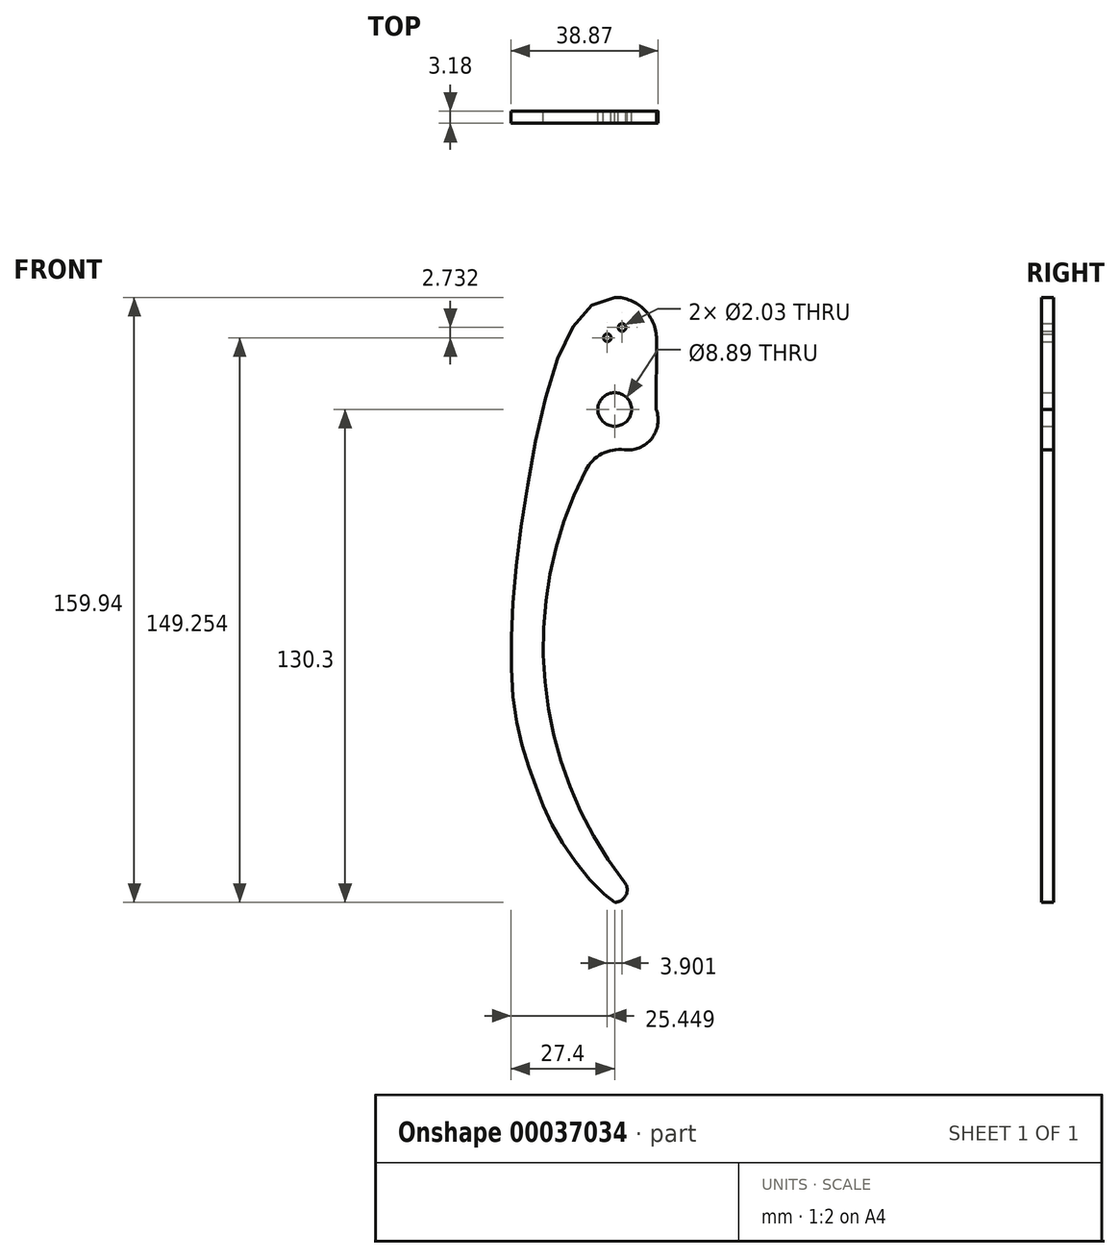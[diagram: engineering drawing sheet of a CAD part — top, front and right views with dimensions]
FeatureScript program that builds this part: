
annotation { "Feature Type Name" : "Feature", "Feature Type Description" : "" }
export const myFeature = defineFeature(function(context is Context, id is Id, definition is map)
    precondition{}
    {
        {
            var Q0;
            Q0=qCreatedBy(makeId("Front.planeOp"),FACE);
            var sketch = newSketch(context, id + "F0", { "sketchPlane" : qUnion([Q0])});
            skLineSegment(sketch, "E0", {"start": v(0, 0) * mm, "end": v(0, -127) * mm, "construction": true});
            skLineSegment(sketch, "E1", {"start": v(0, 0) * mm, "end": v(0, 20.32) * mm, "construction": true});
            skLineSegment(sketch, "E2", {"start": v(11.04, 18.57) * mm, "end": v(10.99, 0) * mm});
            skArc(sketch, "E3", {"start": v(0, -130.3) * mm, "mid": v(2.97, -128.45) * mm, "end": v(2.6, -124.97) * mm});
            skLineSegment(sketch, "E4", {"start": v(-9.53, 0) * mm, "end": v(9.53, 0) * mm, "construction": true});
            skCircle(sketch, "E5", {"center": v(0, 0) * mm, "radius": 4.45 * mm});
            skArc(sketch, "E6", {"start": v(2.54, -10.65) * mm, "mid": v(-3.38, -11.75) * mm, "end": v(-7.62, -16.04) * mm});
            skArc(sketch, "E7", {"start": v(-7.62, -16.04) * mm, "mid": v(-18.45, -72) * mm, "end": v(2.6, -124.97) * mm});
            skLineSegment(sketch, "E8", {"start": v(-1.95, 18.95) * mm, "end": v(1.95, 21.69) * mm, "construction": true});
            skCircle(sketch, "E9", {"center": v(-1.95, 18.95) * mm, "radius": 1.02 * mm});
            skCircle(sketch, "E10", {"center": v(1.95, 21.69) * mm, "radius": 1.02 * mm});
            skFitSpline(sketch, "E11", {"points": [v(0, 29.64) * mm, v(-22.87, -19.28) * mm, v(-26.8, -76.27) * mm, v(-20.77, -99.96) * mm, v(-11.65, -117.92) * mm, v(0, -130.3) * mm], "startDerivative": vector(-153.47, 1.2) * mm, "endDerivative": vector(47.69, -22.62) * mm});
            skLineSegment(sketch, "E12", {"start": v(0, 20.32) * mm, "end": v(0, 29.64) * mm, "construction": true});
            skLineSegment(sketch, "E13", {"start": v(0, -127) * mm, "end": v(0, -130.3) * mm, "construction": true});
            skArc(sketch, "E14", {"start": v(11.04, 18.57) * mm, "mid": v(7.82, 26.4) * mm, "end": v(0, 29.64) * mm});
            skArc(sketch, "E15", {"start": v(2.54, -10.65) * mm, "mid": v(9.75, -7.7) * mm, "end": v(10.99, 0) * mm});
            skSolve(sketch);
        }
        {
            var Q0;
            Q0 = qSketchRegion(id + "F0", true);
            extrude(context, id + "F1", {"entities" : qUnion([Q0]), "depth" : 3.17 * mm});
        }
    });
